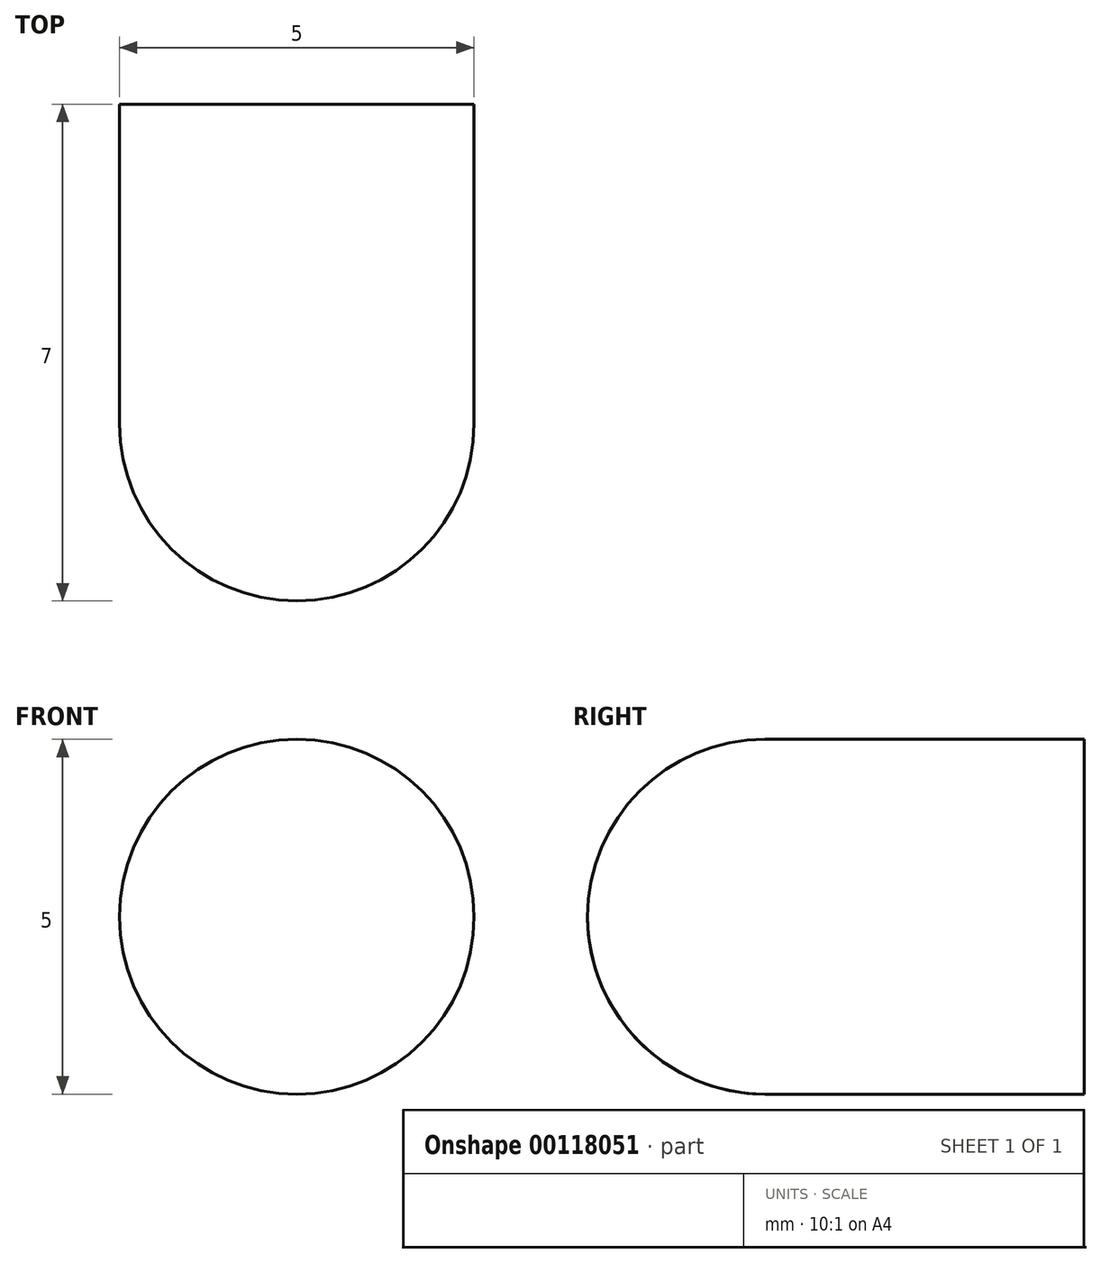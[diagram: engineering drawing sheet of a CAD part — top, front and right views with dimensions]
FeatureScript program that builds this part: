
annotation { "Feature Type Name" : "Feature", "Feature Type Description" : "" }
export const myFeature = defineFeature(function(context is Context, id is Id, definition is map)
    precondition{}
    {
        {
            var Q0;
            Q0=qCreatedBy(makeId("Front.planeOp"),FACE);
            var sketch = newSketch(context, id + "F0", { "sketchPlane" : qUnion([Q0])});
            skCircle(sketch, "E0", {"center": v(0, 0) * mm, "radius": 2.5 * mm});
            skSolve(sketch);
        }
        {
            var Q0;
            Q0 = qSketchRegion(id + "F0", true);
            var Q1;
            Q1=makeQuery(id+"F0.imprint","IMPRINT",FACE,{"disambiguationData":[TD([[makeQuery(id+"F0.imprint","IMPRINT",EDGE,{"derivedFrom":sQuery(id+"F0.wireOp",EDGE,"E0")}),1.0]])]});
            extrude(context, id + "F1", {"entities" : qUnion([Q0, Q1]), "depth" : 7 * mm});
        }
        {
            var Q0;
            Q0=makeQuery(id+"F1.opExtrude","CAP_EDGE",EDGE,{"disambiguationData":[OSD([sQuery(id+"F0.wireOp",EDGE,"E0")])],"isStart":false});
            fillet(context, id + "F2", {"entities" : qUnion([Q0]), "radius" : 2.5 * mm, "tangentPropagation" : true, "allowEdgeOverflow" : false});
        }
    });
